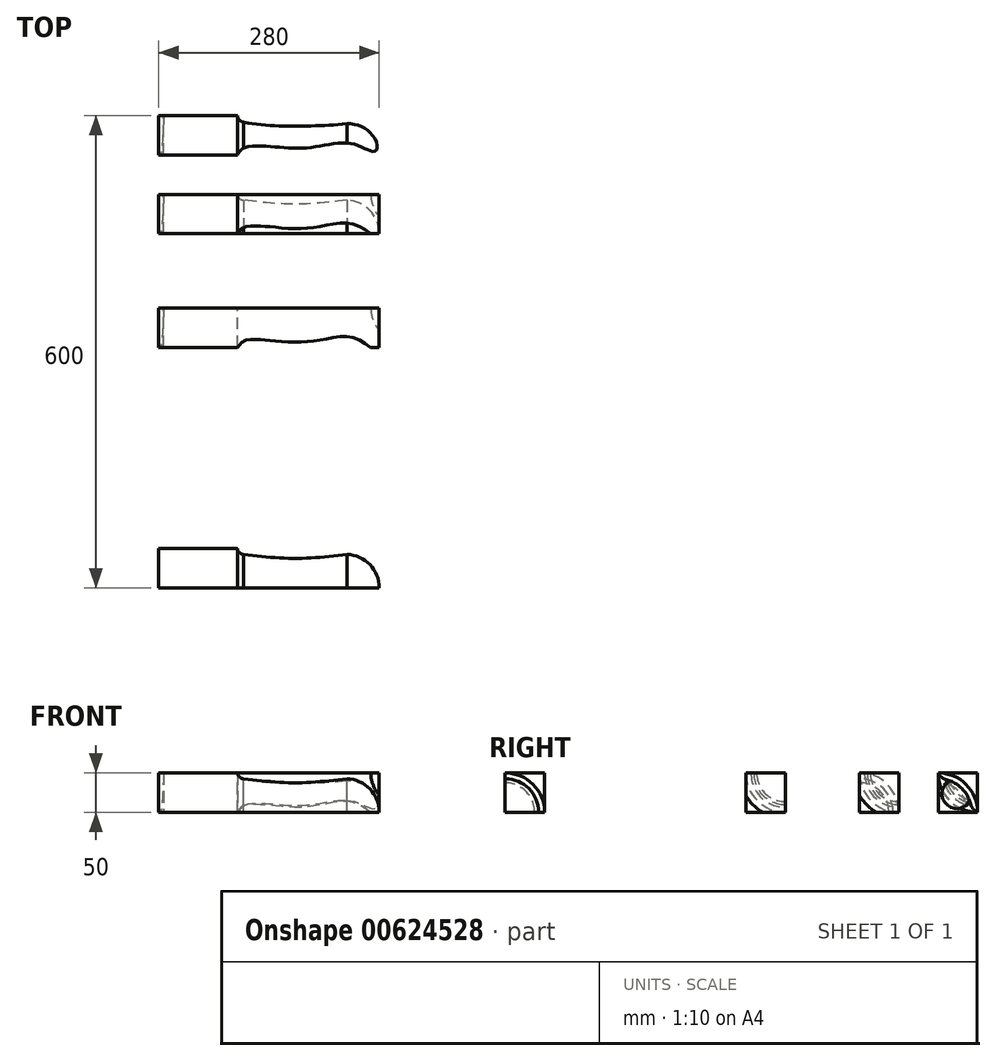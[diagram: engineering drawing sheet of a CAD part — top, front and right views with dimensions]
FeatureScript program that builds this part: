
annotation { "Feature Type Name" : "Feature", "Feature Type Description" : "" }
export const myFeature = defineFeature(function(context is Context, id is Id, definition is map)
    precondition{}
    {
        {
            var Q0;
            Q0=qCreatedBy(makeId("Right.planeOp"),FACE);
            var sketch = newSketch(context, id + "F0", { "sketchPlane" : qUnion([Q0])});
            skLineSegment(sketch, "E0.bottom", {"start": v(0, 0) * mm, "end": v(50, 0) * mm});
            skLineSegment(sketch, "E0.top", {"start": v(0, 50) * mm, "end": v(50, 50) * mm});
            skLineSegment(sketch, "E0.left", {"start": v(0, 0) * mm, "end": v(0, 50) * mm});
            skLineSegment(sketch, "E0.right", {"start": v(50, 0) * mm, "end": v(50, 50) * mm});
            skSolve(sketch);
        }
        {
            var Q0;
            Q0 = qSketchRegion(id + "F0", true);
            extrude(context, id + "F1", {"entities" : qUnion([Q0]), "depth" : 280 * mm, "offsetDistance" : 25 * mm});
        }
        {
            var Q0;
            Q0=makeQuery(id+"F1.opExtrude","SWEPT_FACE",FACE,{"disambiguationData":[OSD([sQuery(id+"F0.wireOp",EDGE,"E0.left")])]});
            var sketch = newSketch(context, id + "F2", { "sketchPlane" : qUnion([Q0])});
            skLineSegment(sketch, "E1", {"start": v(100, 50) * mm, "end": v(100, 0) * mm, "construction": true});
            skArc(sketch, "E2", {"start": v(280, 0) * mm, "mid": v(268.02, 29.64) * mm, "end": v(238.8, 42.61) * mm});
            skArc(sketch, "E3", {"start": v(100, 50) * mm, "mid": v(102.38, 44.76) * mm, "end": v(107.73, 42.61) * mm});
            skLineSegment(sketch, "E4", {"start": v(100, 50) * mm, "end": v(100, 74.83) * mm});
            skLineSegment(sketch, "E5", {"start": v(100, 74.83) * mm, "end": v(280, 74.83) * mm});
            skLineSegment(sketch, "E6", {"start": v(280, 74.83) * mm, "end": v(280, 0) * mm});
            skPoint(sketch, "E7.1.internal.snap0", {"position": v(280, 37.41) * mm});
            skFitSpline(sketch, "E7", {"points": [v(238.8, 42.61) * mm, v(172.96, 37.41) * mm, v(107.73, 42.61) * mm], "startDerivative": vector(-131.54, -15.59) * mm, "endDerivative": vector(-130.62, 15.61) * mm});
            skLineSegment(sketch, "E8", {"start": v(100, 50) * mm, "end": v(43.2, 50) * mm});
            skSolve(sketch);
        }
        {
            var Q0;
            {var subQ2=sQuery(id+"F2.wireOp",EDGE,"E2");Q0=makeQuery(id+"F2.imprint","IMPRINT",FACE,{"disambiguationData":[TD([[makeQuery(id+"F2.imprint","IMPRINT",EDGE,{"derivedFrom":subQ2}),-1.0]])]});}
            var Q1;
            {var subQ0=sQuery(id+"F2.wireOp",EDGE,"E4");Q1=makeQuery(id+"F2.imprint","IMPRINT",FACE,{"disambiguationData":[TD([[makeQuery(id+"F2.imprint","IMPRINT",EDGE,{"derivedFrom":subQ0}),-1.0]])]});}
            var Q2;
            Q2=makeQuery(id+"F2.imprint","IMPRINT",FACE,{"disambiguationData":[TD([[makeQuery(id+"F2.imprint","IMPRINT",EDGE,{"derivedFrom":sQuery(id+"F2.wireOp",EDGE,"E4")}),1.0]])]});
            var Q3;
            Q3=makeQuery(id+"F1.opExtrude","SWEPT_EDGE",EDGE,{"disambiguationData":[OSD([sQuery(id+"F0.wireOp",EDGE,"E0.bottom"),sQuery(id+"F0.wireOp",EDGE,"E0.left")])]});
            revolve(context, id + "F3", {"operationType" : NewBodyOperationType.REMOVE, "entities" : qUnion([Q0, Q1, Q2]), "axis" : qUnion([Q3]), "revolveType" : RevolveType.ONE_DIRECTION, "angle" : 90 * degree});
        }
        {
            var Q0;
            Q0=qCreatedBy(makeId("Right.planeOp"),FACE);
            var sketch = newSketch(context, id + "F4", { "sketchPlane" : qUnion([Q0])});
            skLineSegment(sketch, "E9.bottom", {"start": v(305.7, 0) * mm, "end": v(355.7, 0) * mm});
            skLineSegment(sketch, "E9.top", {"start": v(305.7, 50) * mm, "end": v(355.7, 50) * mm});
            skLineSegment(sketch, "E9.left", {"start": v(305.7, 0) * mm, "end": v(305.7, 50) * mm});
            skLineSegment(sketch, "E9.right", {"start": v(355.7, 0) * mm, "end": v(355.7, 50) * mm});
            skSolve(sketch);
        }
        {
            var Q0;
            Q0 = qSketchRegion(id + "F4", true);
            extrude(context, id + "F5", {"entities" : qUnion([Q0]), "depth" : 280 * mm, "offsetDistance" : 25 * mm});
        }
        {
            var Q0;
            Q0=makeQuery(id+"F5.opExtrude","SWEPT_FACE",FACE,{"disambiguationData":[OSD([sQuery(id+"F4.wireOp",EDGE,"E9.right")])]});
            var sketch = newSketch(context, id + "F6", { "sketchPlane" : qUnion([Q0])});
            skPoint(sketch, "E10.3.internal.snap0", {"position": v(-193.48, 6.38) * mm});
            skPoint(sketch, "E10.4.internal.snap0", {"position": v(-193.48, 8.98) * mm});
            skFitSpline(sketch, "E10", {"points": [v(-280, -7.59) * mm, v(-248.62, 11.86) * mm, v(-209.32, 10.03) * mm, v(-172.92, 6.38) * mm, v(-139.7, 8.98) * mm, v(-120.45, 9.87) * mm, v(-100, 0) * mm], "startDerivative": vector(144.72, 84.36) * mm, "endDerivative": vector(100.14, -210.24) * mm});
            skLineSegment(sketch, "E11", {"start": v(-100.7, -39.31) * mm, "end": v(-280, -39.31) * mm});
            skLineSegment(sketch, "E12", {"start": v(-280, -39.31) * mm, "end": v(-280, 0) * mm});
            skLineSegment(sketch, "E13", {"start": v(-100, 0) * mm, "end": v(-100, 50) * mm, "construction": true});
            skLineSegment(sketch, "E14", {"start": v(-100.7, -39.31) * mm, "end": v(0, -39.31) * mm});
            skLineSegment(sketch, "E15", {"start": v(0, -39.31) * mm, "end": v(-5.95, 0) * mm});
            skLineSegment(sketch, "E16", {"start": v(-10.41, 0) * mm, "end": v(-100, 0) * mm});
            skLineSegment(sketch, "E17", {"start": v(-100.7, -39.31) * mm, "end": v(-90.56, 0) * mm});
            skSolve(sketch);
        }
        {
            var Q0;
            Q0=makeQuery(id+"F6.imprint","IMPRINT",FACE,{"disambiguationData":[TD([[makeQuery(id+"F6.imprint","IMPRINT",EDGE,{"derivedFrom":sQuery(id+"F6.wireOp",EDGE,"wrbUoql8-kTUF-eIMZ-XG7Q-Cp67Qwcvi1Mt")}),1.0]])]});
            var Q1;
            {var subQ0=sQuery(id+"F6.wireOp",EDGE,"E10");var subQ1=makeQuery(id+"F5.opExtrude","SWEPT_EDGE",EDGE,{"disambiguationData":[OSD([sQuery(id+"F4.wireOp",EDGE,"E9.bottom"),sQuery(id+"F4.wireOp",EDGE,"E9.right")])]});var subQ3=makeQuery(id+"F6.imprint","INTERSECT",VERTEX,{"derivedFrom":[subQ1,subQ0]});Q1=makeQuery(id+"F6.imprint","IMPRINT",FACE,{"disambiguationData":[TD([[makeQuery(id+"F6.imprint","IMPRINT",EDGE,{"disambiguationData":[TD([[subQ3,-1.0]])],"derivedFrom":subQ0}),-1.0]])]});}
            var Q2;
            {var subQ3=sQuery(id+"F6.wireOp",EDGE,"E11");Q2=makeQuery(id+"F6.imprint","IMPRINT",FACE,{"disambiguationData":[TD([[makeQuery(id+"F6.imprint","IMPRINT",EDGE,{"derivedFrom":subQ3}),-1.0]])]});}
            var Q3;
            Q3=makeQuery(id+"F6.imprint","IMPRINT",FACE,{"disambiguationData":[TD([[makeQuery(id+"F6.imprint","IMPRINT",EDGE,{"derivedFrom":sQuery(id+"F6.wireOp",EDGE,"E14")}),1.0]])]});
            var Q4;
            Q4=makeQuery(id+"F5.opExtrude","SWEPT_EDGE",EDGE,{"disambiguationData":[OSD([sQuery(id+"F4.wireOp",EDGE,"E9.top"),sQuery(id+"F4.wireOp",EDGE,"E9.right")])]});
            revolve(context, id + "F7", {"operationType" : NewBodyOperationType.REMOVE, "entities" : qUnion([Q0, Q1, Q2, Q3]), "axis" : qUnion([Q4]), "revolveType" : RevolveType.ONE_DIRECTION, "angle" : 90 * degree});
        }
        {
            var Q0;
            Q0=makeQuery(id+"F1.opExtrude","SWEPT_BODY",BODY,{"disambiguationData":[OSD([sQuery(id+"F0.wireOp",EDGE,"E0.bottom"),sQuery(id+"F0.wireOp",EDGE,"E0.top"),sQuery(id+"F0.wireOp",EDGE,"E0.left"),sQuery(id+"F0.wireOp",EDGE,"E0.right")])]});
            var Q1;
            Q1=makeQuery(id+"F5.opExtrude","CAP_EDGE",EDGE,{"disambiguationData":[OSD([sQuery(id+"F4.wireOp",EDGE,"E9.bottom")])],"isStart":true});
            transform(context, id + "F8", {"entities" : qUnion([Q0]), "transformType" : TransformType.TRANSLATION_DISTANCE, "transformDirection" : qUnion([Q1]), "distance" : 400 * mm, "makeCopy" : true});
        }
        {
            var Q0;
            Q0=makeQuery(id+"F5.opExtrude","SWEPT_BODY",BODY,{"disambiguationData":[OSD([sQuery(id+"F4.wireOp",EDGE,"E9.bottom"),sQuery(id+"F4.wireOp",EDGE,"E9.top"),sQuery(id+"F4.wireOp",EDGE,"E9.left"),sQuery(id+"F4.wireOp",EDGE,"E9.right")])]});
            var Q1;
            Q1=makeQuery(id+"F5.opExtrude","CAP_VERTEX",VERTEX,{"disambiguationData":[OSD([sQuery(id+"F4.wireOp",EDGE,"E9.bottom"),sQuery(id+"F4.wireOp",EDGE,"E9.left")])],"isStart":true});
            var Q2;
            Q2=makeQuery(id+"F8.opPattern","COPY",VERTEX,{"derivedFrom":makeQuery(id+"F1.opExtrude","CAP_VERTEX",VERTEX,{"disambiguationData":[OSD([sQuery(id+"F0.wireOp",EDGE,"E0.bottom"),sQuery(id+"F0.wireOp",EDGE,"E0.left")])],"isStart":true}),"instanceName":"1"});
            transform(context, id + "F9", {"entities" : qUnion([Q0]), "transformType" : TransformType.TRANSLATION_ENTITY, "oppositeDirectionEntity" : false, "transformLine" : qUnion([Q1, Q2]), "makeCopy" : true});
        }
        {
            var Q0;
            Q0=makeQuery(id+"F8.opPattern","COPY",BODY,{"derivedFrom":makeQuery(id+"F1.opExtrude","SWEPT_BODY",BODY,{"disambiguationData":[OSD([sQuery(id+"F0.wireOp",EDGE,"E0.bottom"),sQuery(id+"F0.wireOp",EDGE,"E0.top"),sQuery(id+"F0.wireOp",EDGE,"E0.left"),sQuery(id+"F0.wireOp",EDGE,"E0.right")])]}),"instanceName":"1"});
            var Q1;
            Q1=makeQuery(id+"F9.opPattern","COPY",BODY,{"derivedFrom":makeQuery(id+"F5.opExtrude","SWEPT_BODY",BODY,{"disambiguationData":[OSD([sQuery(id+"F4.wireOp",EDGE,"E9.bottom"),sQuery(id+"F4.wireOp",EDGE,"E9.top"),sQuery(id+"F4.wireOp",EDGE,"E9.left"),sQuery(id+"F4.wireOp",EDGE,"E9.right")])]}),"instanceName":"1"});
            var Q2;
            Q2=makeQuery(id+"F9.opPattern","COPY",EDGE,{"derivedFrom":makeQuery(id+"F5.opExtrude","CAP_EDGE",EDGE,{"disambiguationData":[OSD([sQuery(id+"F4.wireOp",EDGE,"E9.bottom")])],"isStart":true}),"instanceName":"1"});
            transform(context, id + "F10", {"entities" : qUnion([Q0, Q1]), "transformType" : TransformType.TRANSLATION_DISTANCE, "transformDirection" : qUnion([Q2]), "distance" : 50 * mm, "makeCopy" : false});
        }
        {
            var Q0;
            Q0=makeQuery(id+"F8.opPattern","COPY",BODY,{"derivedFrom":makeQuery(id+"F1.opExtrude","SWEPT_BODY",BODY,{"disambiguationData":[OSD([sQuery(id+"F0.wireOp",EDGE,"E0.bottom"),sQuery(id+"F0.wireOp",EDGE,"E0.top"),sQuery(id+"F0.wireOp",EDGE,"E0.left"),sQuery(id+"F0.wireOp",EDGE,"E0.right")])]}),"instanceName":"1"});
            var Q1;
            Q1=makeQuery(id+"F9.opPattern","COPY",BODY,{"derivedFrom":makeQuery(id+"F5.opExtrude","SWEPT_BODY",BODY,{"disambiguationData":[OSD([sQuery(id+"F4.wireOp",EDGE,"E9.bottom"),sQuery(id+"F4.wireOp",EDGE,"E9.top"),sQuery(id+"F4.wireOp",EDGE,"E9.left"),sQuery(id+"F4.wireOp",EDGE,"E9.right")])]}),"instanceName":"1"});
            var Q2;
            Q2=makeQuery(id+"F5.opExtrude","CAP_EDGE",EDGE,{"disambiguationData":[OSD([sQuery(id+"F4.wireOp",EDGE,"E9.bottom")])],"isStart":true});
            transform(context, id + "F11", {"entities" : qUnion([Q0, Q1]), "transformType" : TransformType.TRANSLATION_DISTANCE, "transformDirection" : qUnion([Q2]), "distance" : 100 * mm, "makeCopy" : true});
        }
        {
            var Q0;
            Q0=makeQuery(id+"F11.opPattern","COPY",BODY,{"derivedFrom":makeQuery(id+"F9.opPattern","COPY",BODY,{"derivedFrom":makeQuery(id+"F5.opExtrude","SWEPT_BODY",BODY,{"disambiguationData":[OSD([sQuery(id+"F4.wireOp",EDGE,"E9.bottom"),sQuery(id+"F4.wireOp",EDGE,"E9.top"),sQuery(id+"F4.wireOp",EDGE,"E9.left"),sQuery(id+"F4.wireOp",EDGE,"E9.right")])]}),"instanceName":"1"}),"instanceName":"1"});
            var Q1;
            Q1=makeQuery(id+"F11.opPattern","COPY",BODY,{"derivedFrom":makeQuery(id+"F8.opPattern","COPY",BODY,{"derivedFrom":makeQuery(id+"F1.opExtrude","SWEPT_BODY",BODY,{"disambiguationData":[OSD([sQuery(id+"F0.wireOp",EDGE,"E0.bottom"),sQuery(id+"F0.wireOp",EDGE,"E0.top"),sQuery(id+"F0.wireOp",EDGE,"E0.left"),sQuery(id+"F0.wireOp",EDGE,"E0.right")])]}),"instanceName":"1"}),"instanceName":"1"});
            booleanBodies(context, id + "F12", {"operationType" : BooleanOperationType.INTERSECTION, "tools" : qUnion([Q0, Q1])});
        }
    });
